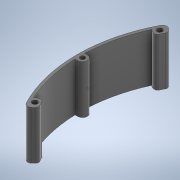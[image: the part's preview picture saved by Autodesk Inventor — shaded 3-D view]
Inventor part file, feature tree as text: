
AUTODESK INVENTOR PART (.ipt)
format: ipt  version: 2020 (Build 240168000, 168)  size: 1,268,736 bytes
history: native  units: mm
features: extrude x12, sketch x9, projected_geometry x9, other x3, fillet x2
ambient origin geometry x8: Origin, YZ Plane, XZ Plane, XY Plane, X Axis, Y Axis, Z Axis, Center Point
bodies: Body1 (feature_tree)
feature tree (35):
  other  "Твердое тело1"
  extrude  "outer"  TaperAngle=45.0deg  [1 undecoded]
  extrude  "inner"  Depth=7.0mm
  sketch  "Эскиз3"
  extrude  "Выдавливание3"  Depth=20.0mm
  extrude  "Выдавливание4"  Depth=7.0mm
  sketch  "Эскиз4"
  extrude  "Выдавливание5"  Depth=3.2mm
  extrude  "Выдавливание6"  Depth=59.0mm
  sketch  "Эскиз5"
  extrude  "Выдавливание7"  Depth=83.0mm
  extrude  "Выдавливание8"  Depth=69.0mm
  sketch  "Эскиз6"
  extrude  "Выдавливание9"  Depth=55.0mm
  extrude  "Выдавливание10"  Depth=3.0mm
  fillet  "Сопряжение1"  Radius=8.0mm
  other  "РабПлоскость2"
  sketch  "Эскиз8"
  extrude  "Выдавливание11"  Depth=5.0mm
  fillet  "Сопряжение2"  Radius=2.0mm
  sketch  "3D эскиз1"
  extrude  "Выдавливание12"  Depth=40.0mm TaperAngle=360.0deg
  sketch  "Эскиз1"
  sketch  "Эскиз2"
  projected_geometry  "Спроецированная петля1"
  projected_geometry  "Спроецированная петля2"
  projected_geometry  "Спроецированная петля3"
  projected_geometry  "Спроецированная петля4"
  projected_geometry  "Спроецированная петля5"
  projected_geometry  "Спроецированная петля8"
  projected_geometry  "Спроецированная петля9"
  projected_geometry  "Спроецированная петля10"
  other  "Проецирование на поверхность1"
  sketch  "Эскиз10"
  projected_geometry  "Спроецированная петля11"
note: 1 required parameter value undecoded (feature->parameter linkage not recoverable at this tier; creation-order binding heuristic only, values carry confidence <= 0.55)
